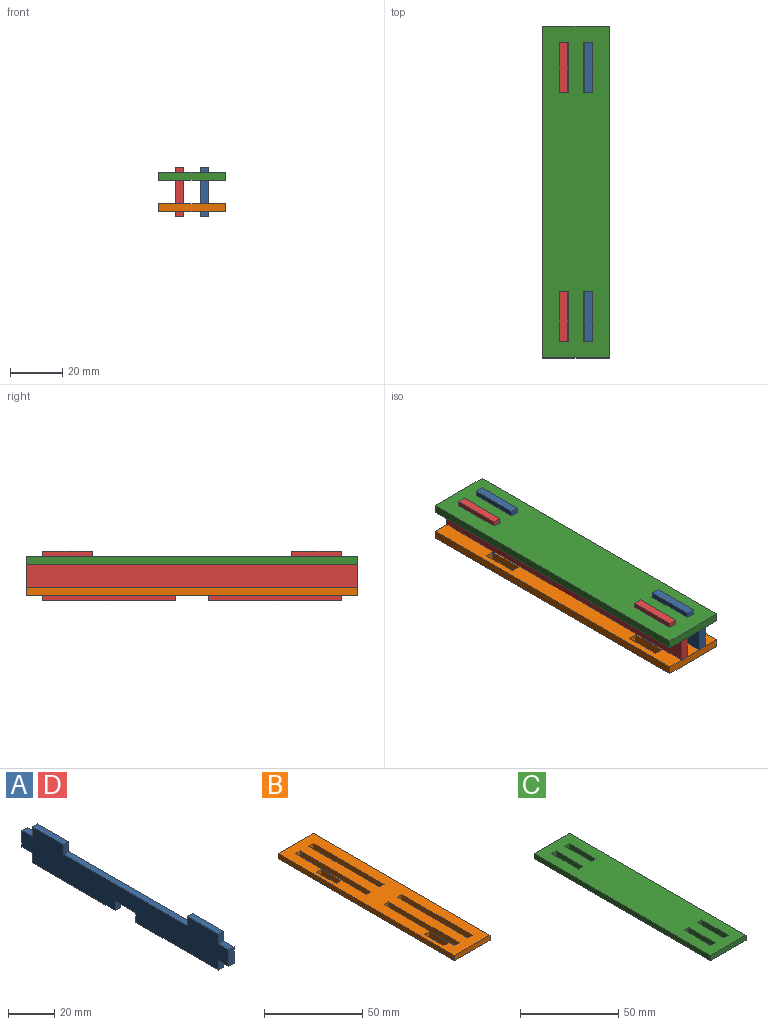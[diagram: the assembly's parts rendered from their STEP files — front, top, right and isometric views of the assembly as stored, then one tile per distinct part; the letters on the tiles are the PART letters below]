
ASSEMBLY  parts=4 mates=9
PART A: 22 faces, bbox 3.2x127x19.1 mm
  f0: plane 5.08x3.18mm, normal (0,1,0), area 16.1mm2, adj f1,f19,f20,f21
  f1: plane 19.05x3.18mm, normal (0,0,1), area 60.5mm2, adj f0,f2,f20,f21
  f2: plane 5.08x3.18mm, normal (0,-1,0), area 16.1mm2, adj f1,f3,f20,f21
  f3: plane 76.2x3.18mm, normal (0,0,1), area 241.9mm2, adj f2,f4,f20,f21
  f4: plane 5.08x3.18mm, normal (0,1,0), area 16.1mm2, adj f3,f5,f20,f21
  f5: plane 19.05x3.18mm, normal (0,0,1), area 60.5mm2, adj f4,f6,f20,f21
  f6: plane 5.08x3.18mm, normal (0,-1,0), area 16.1mm2, adj f5,f7,f20,f21
  f7: plane 6.35x3.18mm, normal (0,0,1), area 20.2mm2, adj f6,f8,f20,f21
  f8: plane 8.89x3.18mm, normal (0,-1,0), area 28.2mm2, adj f7,f9,f20,f21
  f9: plane 6.35x3.18mm, normal (0,0,-1), area 20.2mm2, adj f8,f10,f20,f21
  f10: plane 5.08x3.18mm, normal (0,-1,0), area 16.1mm2, adj f9,f11,f20,f21
  f11: plane 50.8x3.18mm, normal (0,0,-1), area 161.3mm2, adj f10,f12,f20,f21
  f12: plane 5.08x3.18mm, normal (0,1,0), area 16.1mm2, adj f11,f13,f20,f21
  f13: plane 12.7x3.18mm, normal (0,0,-1), area 40.3mm2, adj f12,f14,f20,f21
  f14: plane 5.08x3.18mm, normal (0,-1,0), area 16.1mm2, adj f13,f15,f20,f21
  f15: plane 50.8x3.18mm, normal (0,0,-1), area 161.3mm2, adj f14,f16,f20,f21
  f16: plane 5.08x3.18mm, normal (0,1,0), area 16.1mm2, adj f15,f17,f20,f21
  f17: plane 6.35x3.18mm, normal (0,0,-1), area 20.2mm2, adj f16,f18,f20,f21
  f18: plane 8.89x3.18mm, normal (0,1,0), area 28.2mm2, adj f17,f19,f20,f21
  f19: plane 6.35x3.18mm, normal (0,0,1), area 20.2mm2, adj f0,f18,f20,f21
  f20: plane 127x19.05mm, normal (1,0,0), area 1838.7mm2, adj f0,f1,f2,f3,f4,f5,f6,f7
  f21: plane 127x19.05mm, normal (-1,0,0), area 1838.7mm2, adj f0,f1,f2,f3,f4,f5,f6,f7
PART B: 30 faces, bbox 25.4x127x3.2 mm
  f0: plane 3.3x3.18mm, normal (0,-1,0), area 10.5mm2, adj f1,f27,f28,f29
  f1: plane 50.8x3.18mm, normal (-1,0,0), area 161.3mm2, adj f0,f2,f28,f29
  f2: plane 3.3x3.18mm, normal (0,1,0), area 10.5mm2, adj f1,f27,f28,f29
  f3: plane 13.97x3.18mm, normal (1,0,0), area 44.4mm2, adj f4,f21,f28,f29
  f4: plane 3.3x3.18mm, normal (0,-1,0), area 10.5mm2, adj f3,f5,f28,f29
  f5: plane 13.97x3.18mm, normal (-1,0,0), area 44.4mm2, adj f4,f21,f28,f29
  f6: plane 13.97x3.18mm, normal (1,0,0), area 44.4mm2, adj f7,f22,f28,f29
  f7: plane 3.3x3.18mm, normal (0,-1,0), area 10.5mm2, adj f6,f8,f28,f29
  f8: plane 13.97x3.18mm, normal (-1,0,0), area 44.4mm2, adj f7,f22,f28,f29
  f9: plane 3.3x3.18mm, normal (0,1,0), area 10.5mm2, adj f10,f23,f28,f29
  f10: plane 50.8x3.18mm, normal (1,0,0), area 161.3mm2, adj f9,f11,f28,f29
  f11: plane 3.3x3.18mm, normal (0,-1,0), area 10.5mm2, adj f10,f23,f28,f29
  f12: plane 3.3x3.18mm, normal (0,-1,0), area 10.5mm2, adj f13,f24,f28,f29
  f13: plane 50.8x3.18mm, normal (-1,0,0), area 161.3mm2, adj f12,f14,f28,f29
  f14: plane 3.3x3.18mm, normal (0,1,0), area 10.5mm2, adj f13,f24,f28,f29
  f15: plane 50.8x3.18mm, normal (1,0,0), area 161.3mm2, adj f16,f25,f28,f29
  f16: plane 3.3x3.18mm, normal (0,-1,0), area 10.5mm2, adj f15,f17,f28,f29
  f17: plane 50.8x3.18mm, normal (-1,0,0), area 161.3mm2, adj f16,f25,f28,f29
  f18: plane 127x3.18mm, normal (-1,0,0), area 403.2mm2, adj f19,f26,f28,f29
  f19: plane 25.4x3.18mm, normal (0,-1,0), area 80.6mm2, adj f18,f20,f28,f29
  f20: plane 127x3.18mm, normal (1,0,0), area 403.2mm2, adj f19,f26,f28,f29
  f21: plane 3.3x3.18mm, normal (0,1,0), area 10.5mm2, adj f3,f5,f28,f29
  f22: plane 3.3x3.18mm, normal (0,1,0), area 10.5mm2, adj f6,f8,f28,f29
  f23: plane 50.8x3.18mm, normal (-1,0,0), area 161.3mm2, adj f9,f11,f28,f29
  f24: plane 50.8x3.18mm, normal (1,0,0), area 161.3mm2, adj f12,f14,f28,f29
  f25: plane 3.3x3.18mm, normal (0,1,0), area 10.5mm2, adj f15,f17,f28,f29
  f26: plane 25.4x3.18mm, normal (0,1,0), area 80.6mm2, adj f18,f20,f28,f29
  f27: plane 50.8x3.18mm, normal (1,0,0), area 161.3mm2, adj f0,f2,f28,f29
  f28: plane 127x25.4mm, normal (0,0,1), area 2462.6mm2, adj f0,f1,f2,f3,f4,f5,f6,f7
  f29: plane 127x25.4mm, normal (0,0,-1), area 2462.6mm2, adj f0,f1,f2,f3,f4,f5,f6,f7
PART C: 22 faces, bbox 25.4x127x3.2 mm
  f0: plane 3.3x3.18mm, normal (0,-1,0), area 10.5mm2, adj f1,f19,f20,f21
  f1: plane 19.18x3.18mm, normal (-1,0,0), area 60.9mm2, adj f0,f2,f20,f21
  f2: plane 3.3x3.18mm, normal (0,1,0), area 10.5mm2, adj f1,f19,f20,f21
  f3: plane 3.3x3.18mm, normal (0,1,0), area 10.5mm2, adj f4,f15,f20,f21
  f4: plane 19.18x3.18mm, normal (1,0,0), area 60.9mm2, adj f3,f5,f20,f21
  f5: plane 3.3x3.18mm, normal (0,-1,0), area 10.5mm2, adj f4,f15,f20,f21
  f6: plane 3.3x3.18mm, normal (0,-1,0), area 10.5mm2, adj f7,f16,f20,f21
  f7: plane 19.18x3.18mm, normal (-1,0,0), area 60.9mm2, adj f6,f8,f20,f21
  f8: plane 3.3x3.18mm, normal (0,1,0), area 10.5mm2, adj f7,f16,f20,f21
  f9: plane 19.18x3.18mm, normal (1,0,0), area 60.9mm2, adj f10,f17,f20,f21
  f10: plane 3.3x3.18mm, normal (0,-1,0), area 10.5mm2, adj f9,f11,f20,f21
  f11: plane 19.18x3.18mm, normal (-1,0,0), area 60.9mm2, adj f10,f17,f20,f21
  f12: plane 127x3.18mm, normal (-1,0,0), area 403.2mm2, adj f13,f18,f20,f21
  f13: plane 25.4x3.18mm, normal (0,-1,0), area 80.6mm2, adj f12,f14,f20,f21
  f14: plane 127x3.18mm, normal (1,0,0), area 403.2mm2, adj f13,f18,f20,f21
  f15: plane 19.18x3.18mm, normal (-1,0,0), area 60.9mm2, adj f3,f5,f20,f21
  f16: plane 19.18x3.18mm, normal (1,0,0), area 60.9mm2, adj f6,f8,f20,f21
  f17: plane 3.3x3.18mm, normal (0,1,0), area 10.5mm2, adj f9,f11,f20,f21
  f18: plane 25.4x3.18mm, normal (0,1,0), area 80.6mm2, adj f12,f14,f20,f21
  f19: plane 19.18x3.18mm, normal (1,0,0), area 60.9mm2, adj f0,f2,f20,f21
  f20: plane 127x25.4mm, normal (0,0,1), area 2972.5mm2, adj f0,f1,f2,f3,f4,f5,f6,f7
  f21: plane 127x25.4mm, normal (0,0,-1), area 2972.5mm2, adj f0,f1,f2,f3,f4,f5,f6,f7
PART D: same geometry as A
PLACE A t=(-25.56,158.16,46.79)mm
PLACE B t=(-41.43,31.16,29.64)mm
PLACE C t=(-41.43,31.16,41.71)mm
PLACE D t=(-35.08,158.16,46.79)mm
MATE planar A.f20 <-> C.f7  axis (1,0,0) through (-22.38,94.66,36.04)mm
MATE planar D.f21 <-> C.f9  axis (-1,0,0) through (-35.08,94.66,36.04)mm
MATE planar A.f6 <-> C.f8  axis (0,-1,0) through (-23.97,37.51,44.25)mm
MATE planar D.f0 <-> C.f10  axis (0,1,0) through (-33.49,151.81,44.25)mm
MATE planar A.f3 <-> C.f21  axis (0,0,1) through (-23.97,94.66,41.71)mm
MATE planar B.f28 <-> D.f13  axis (0,0,1) through (-28.41,94.94,32.82)mm
MATE planar B.f19 <-> C.f13  axis (0,-1,0) through (-28.73,31.16,31.23)mm
MATE planar B.f20 <-> C.f14  axis (1,0,0) through (-16.03,94.66,31.23)mm
MATE planar C.f21 <-> D.f3  axis (0,0,-1) through (-28.73,94.66,41.71)mm
